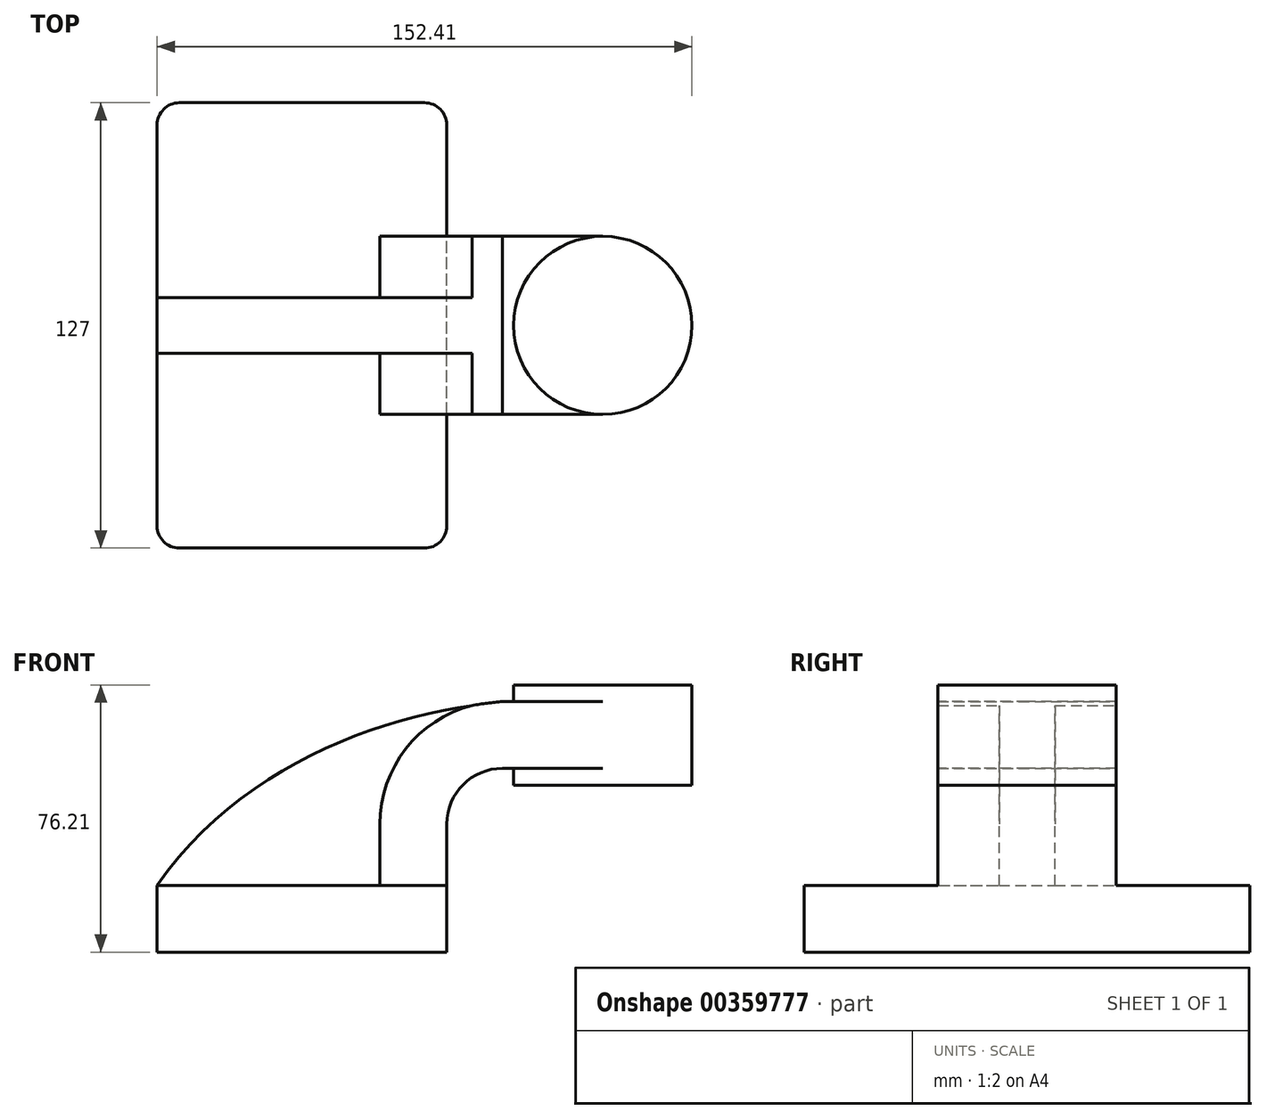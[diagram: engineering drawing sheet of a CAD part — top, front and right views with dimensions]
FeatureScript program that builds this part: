
annotation { "Feature Type Name" : "Feature", "Feature Type Description" : "" }
export const myFeature = defineFeature(function(context is Context, id is Id, definition is map)
    precondition{}
    {
        {
            var Q0;
            Q0=qCreatedBy(makeId("Front.planeOp"),FACE);
            var sketch = newSketch(context, id + "F0", { "sketchPlane" : qUnion([Q0])});
            skLineSegment(sketch, "E0.bottom", {"start": v(41.28, -9.52) * mm, "end": v(-41.28, -9.53) * mm});
            skLineSegment(sketch, "E0.top", {"start": v(41.28, 9.53) * mm, "end": v(-41.28, 9.52) * mm});
            skLineSegment(sketch, "E0.left", {"start": v(41.28, -9.52) * mm, "end": v(41.28, 9.53) * mm});
            skLineSegment(sketch, "E0.right", {"start": v(-41.28, -9.53) * mm, "end": v(-41.28, 9.52) * mm});
            skPoint(sketch, "E0.middle", {"position": v(0, 0) * mm});
            skLineSegment(sketch, "E1.bottom", {"start": v(111.12, 38.1) * mm, "end": v(60.32, 38.1) * mm});
            skLineSegment(sketch, "E1.top", {"start": v(111.12, 66.68) * mm, "end": v(60.32, 66.68) * mm});
            skLineSegment(sketch, "E1.left", {"start": v(111.12, 38.1) * mm, "end": v(111.12, 66.68) * mm});
            skLineSegment(sketch, "E1.right", {"start": v(60.32, 38.1) * mm, "end": v(60.32, 66.68) * mm});
            skPoint(sketch, "E1.middle", {"position": v(85.72, 52.39) * mm});
            skLineSegment(sketch, "E2", {"start": v(41.28, 9.53) * mm, "end": v(41.28, 27) * mm});
            skArc(sketch, "E3", {"start": v(41.28, 27) * mm, "mid": v(45.92, 38.23) * mm, "end": v(57.15, 42.88) * mm});
            skLineSegment(sketch, "E4", {"start": v(57.15, 42.88) * mm, "end": v(85.72, 42.88) * mm});
            skPoint(sketch, "E5", {"position": v(85.72, 38.1) * mm});
            skLineSegment(sketch, "E6.0", {"start": v(57.15, 61.93) * mm, "end": v(85.72, 61.93) * mm});
            skArc(sketch, "E6.1", {"start": v(22.23, 27) * mm, "mid": v(32.45, 51.7) * mm, "end": v(57.15, 61.93) * mm});
            skLineSegment(sketch, "E6.2", {"start": v(22.23, 9.53) * mm, "end": v(22.23, 27) * mm});
            skLineSegment(sketch, "E7", {"start": v(85.72, 38.1) * mm, "end": v(85.72, 66.68) * mm});
            skFitSpline(sketch, "E8", {"points": [v(-41.28, 9.52) * mm, v(57.15, 61.93) * mm], "startDerivative": vector(74.36, 106.19) * mm, "endDerivative": vector(97.98, 9.75) * mm});
            skSolve(sketch);
        }
        {
            var Q0;
            Q0=makeQuery(id+"F0.imprint","IMPRINT",FACE,{"disambiguationData":[TD([[makeQuery(id+"F0.imprint","IMPRINT",EDGE,{"derivedFrom":sQuery(id+"F0.wireOp",EDGE,"E0.bottom")}),-1.0]])]});
            extrude(context, id + "F1", {"entities" : qUnion([Q0]), "endBound" : BoundingType.SYMMETRIC, "depth" : 127 * mm});
        }
        {
            var Q0;
            {var subQ1=sQuery(id+"F0.wireOp",EDGE,"E2");Q0=makeQuery(id+"F0.imprint","IMPRINT",FACE,{"disambiguationData":[TD([[makeQuery(id+"F0.imprint","IMPRINT",EDGE,{"derivedFrom":subQ1}),1.0]])]});}
            var Q1;
            {var subQ0=sQuery(id+"F0.wireOp",EDGE,"E4");var subQ1=sQuery(id+"F0.wireOp",EDGE,"E1.right");var subQ2=makeQuery(id+"F0.imprint","INTERSECT",VERTEX,{"derivedFrom":[subQ1,subQ0]});Q1=makeQuery(id+"F0.imprint","IMPRINT",FACE,{"disambiguationData":[TD([[makeQuery(id+"F0.imprint","IMPRINT",EDGE,{"disambiguationData":[TD([[subQ2,-1.0]])],"derivedFrom":subQ1}),-1.0]])]});}
            extrude(context, id + "F2", {"entities" : qUnion([Q0, Q1]), "operationType" : NewBodyOperationType.ADD, "endBound" : BoundingType.SYMMETRIC, "depth" : 50.8 * mm});
        }
        {
            var Q0;
            {var subQ3=sQuery(id+"F0.wireOp",EDGE,"E6.2");Q0=makeQuery(id+"F0.imprint","IMPRINT",FACE,{"disambiguationData":[TD([[makeQuery(id+"F0.imprint","IMPRINT",EDGE,{"derivedFrom":subQ3}),1.0]])]});}
            extrude(context, id + "F3", {"entities" : qUnion([Q0]), "operationType" : NewBodyOperationType.ADD, "endBound" : BoundingType.SYMMETRIC, "depth" : 15.88 * mm});
        }
        {
            var Q0;
            Q0=makeQuery(id+"F1.opExtrude","CAP_EDGE",EDGE,{"disambiguationData":[OSD([sQuery(id+"F0.wireOp",EDGE,"E0.left")])],"isStart":false});
            var Q1;
            Q1=makeQuery(id+"F1.opExtrude","CAP_EDGE",EDGE,{"disambiguationData":[OSD([sQuery(id+"F0.wireOp",EDGE,"E0.right")])],"isStart":false});
            var Q2;
            Q2=makeQuery(id+"F1.opExtrude","CAP_EDGE",EDGE,{"disambiguationData":[OSD([sQuery(id+"F0.wireOp",EDGE,"E0.right")])],"isStart":true});
            var Q3;
            Q3=makeQuery(id+"F1.opExtrude","CAP_EDGE",EDGE,{"disambiguationData":[OSD([sQuery(id+"F0.wireOp",EDGE,"E0.left")])],"isStart":true});
            fillet(context, id + "F4", {"entities" : qUnion([Q0, Q1, Q2, Q3]), "radius" : 6.35 * mm, "tangentPropagation" : true, "allowEdgeOverflow" : false});
        }
        {
            var Q0;
            {var subQ0=sQuery(id+"F0.wireOp",EDGE,"E1.left");Q0=makeQuery(id+"F0.imprint","IMPRINT",FACE,{"disambiguationData":[TD([[makeQuery(id+"F0.imprint","IMPRINT",EDGE,{"derivedFrom":subQ0}),1.0]])]});}
            var Q1;
            Q1=sQuery(id+"F0.wireOp",EDGE,"E7");
            revolve(context, id + "F5", {"operationType" : NewBodyOperationType.ADD, "entities" : qUnion([Q0]), "axis" : qUnion([Q1]), "revolveType" : RevolveType.FULL});
        }
    });
